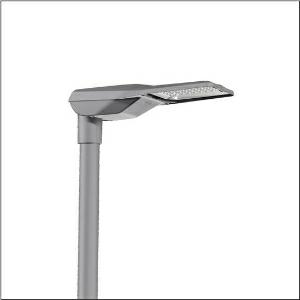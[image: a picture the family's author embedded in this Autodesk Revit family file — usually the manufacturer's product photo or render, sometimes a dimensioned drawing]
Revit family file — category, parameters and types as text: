
# Revit family: streetlight_sl_21_iq_mini___p0_5a_5xe2v31g08jb_8467
name_source: partatom
category: Lighting Fixtures
units: mm (PartAtom-declared; Revit-internal decimal feet)

## family parameters
Cut with Voids When Loaded = No
Host = Face
Light Source = No
Part Type = Normal
Room Calculation Point = No
Round Connector Dimension = Use Diameter
Shared = No

## types (1)
- --- (1 x LED, 10640 lm, 71.6 W, 3000K)
    Apparent Load = 72 VA
    CIE Flux Codes = 37 73 96 100 100
    Color Rendering = 70
    Color Temperature = 3000K
    Default Elevation = 1800 mm
    Description = Streetlight SL 21 iQ mini, mast luminaire, primary light control with lens, of PMMA, primary optical cover: cover, of toughened safety glass, transparent, light distribution: P0.5a, light emission: direct distribution, primary light characteristic: asymmetric, installation type: post-top, side-entry, LED, High Power LED, rated luminous flux: 10.640lm, luminous efficacy: 149lm/W, light colour: 730, colour temperature: 3000K, control gear: iQ Street-Remote, control: pre-setting: linear dimming characteristic, Street-Remote, Auto-Match, Temp-Guard, Lumen-Switch, Night-Set, Smart-Wire, Light-Fading, Desk-Remote (wireless, voltage-free reading and setting of iQ features in the workshop via application-optimized NFC function/RFID function), optimised constant luminous flux control (CLO 2.0), mains connection: 220..240V, AC, 50/60Hz, start of lifetime: 72W, end of service life: 75W, reduction: 33W, luminaire housing, of diecast aluminium, powder-coated, Siteco® metallic grey (DB 702S), corrosivity category C5 mid according to DIN EN ISO 12944, please order mast flange separately, inclination adjustable: 0°, 5°, 10°, 15°, sealing non-destructively replaceable, multi-level sealing system, length: 628mm, width: 235mm, height: 110mm, mast flange for spigot size: 42mm (side-entry): 5XC10008XM4, 60/48mm (side-entry/post-top): 5XC10108XM2, 76/60mm (side-entry/post-top): 5XC10108XM1, mounting height: 4..8m, protection rating (complete): IP66, insulation class (complete): insulation class II (safety insulation), certification: CE, ENEC, ENEC+, VDE, impact resistance: IK10, permissible operating ambient temperature for outdoor applications: -40..+50°C, standard-compliant lighting for roads and squares, packaging unit: 1 piece

Light Distribution: P0.5a
    Height = 110 mm
    Lamp = 1 x LED
    Lamp Light Flux = 10640 lm
    Lamp Power = 71.6 W
    Lamp count = 1
    Length = 625 mm
    Luminous efficacy = 149 lm/W
    Manufacturer = Siteco
    ModVariant = No
    Model = 5XE2V31G08JB
    Number of Poles = 1
    OnlyDefault = Yes
    Power Factor = 1
    Product Name = Streetlight SL 21 iQ mini | P0.5a
    Product group = mast luminaire | pylon top
    ProductGroupID = 6100
    Protection Class = Protection class II
    Protection Degree = IP 66
    RLX_Detail_Level = 1
    RLX_Emergency_Light_Flux = 0 lm
    RLX_Emergency_Type = 0
    RLX_Emergency_Type_DB = No
    RlxData = <blob elided: 26073 chars, md5=277b5349>
    Socket = socket
    Standby Power = 0 W
    System Light Flux = 10640 lm
    System Power = 72 W
    Type Comments = factory setting: luminous flux: 100 % | dim-lin: 254 | 746 mA
    Type Image = l_1003519.jpg
    URL = http://relux.com
    VarID = @adj_069198
    Voltage = 0 V
    Weight = 0.00 kg
    Width = 234 mm

## geometry (parser evidence)
native form markers: Blend x4, Sweep x11
no freeform markers — native parametric forms only
